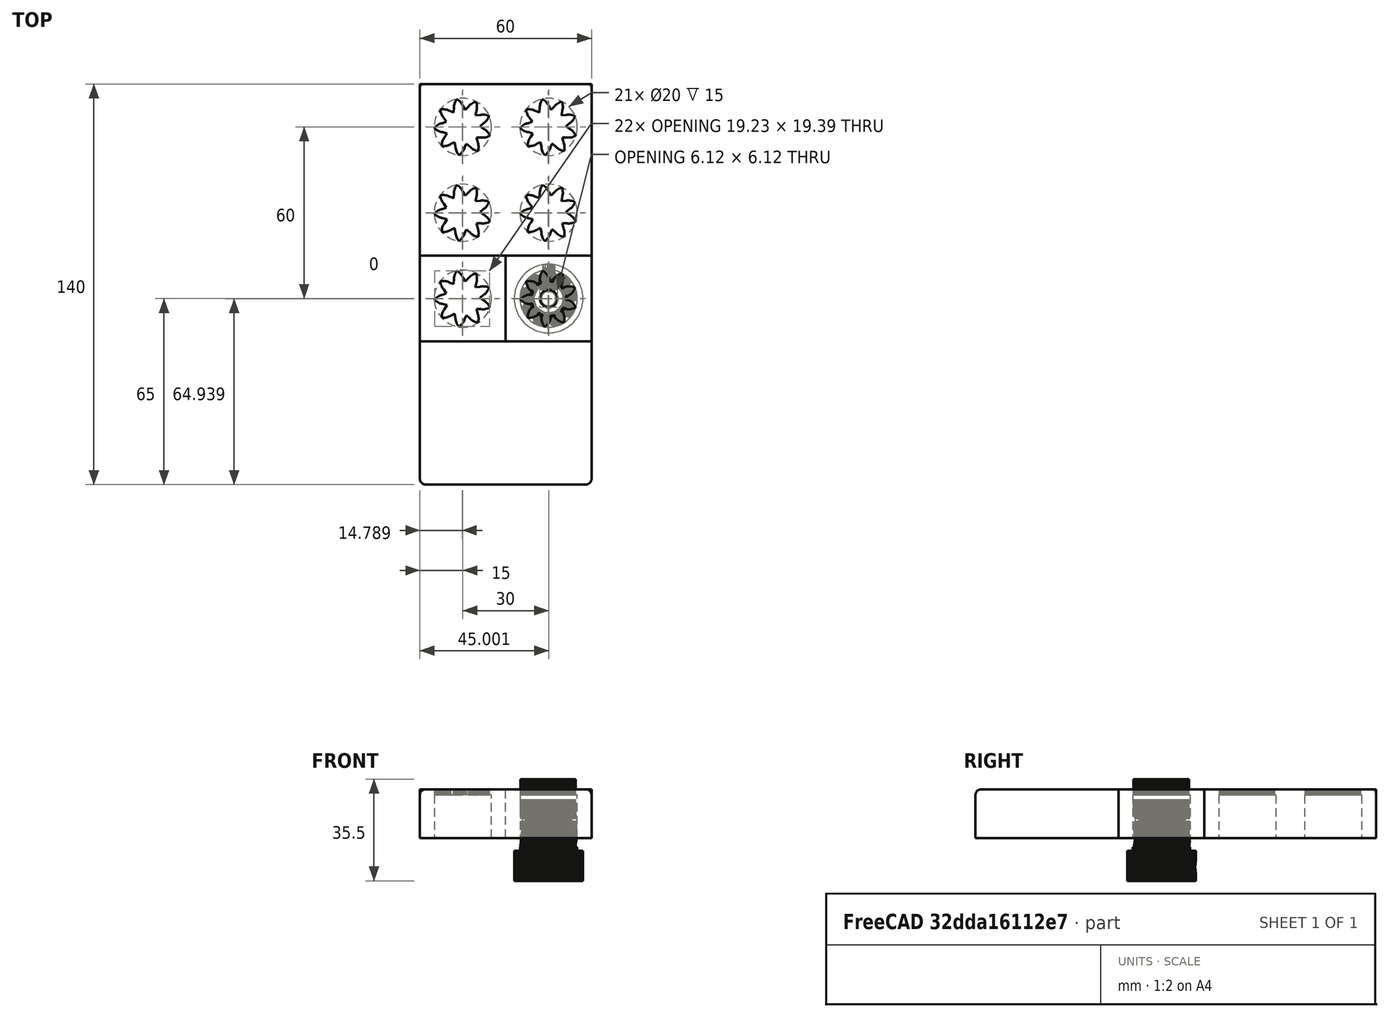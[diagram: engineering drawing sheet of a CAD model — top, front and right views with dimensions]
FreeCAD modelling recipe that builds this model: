
FCSTD DOCUMENT  (FreeCAD 0.17R12018 (Git))
Label: HerringBone6shooter
License: All rights reserved
LicenseURL: http://en.wikipedia.org/wiki/All_rights_reserved
objects: Part::Feature×8, Part::FeaturePython×4, PartDesign::Body×4, Part::MultiFuse×4, PartDesign::Pad×2, Part::Box×2, Sketcher::SketchObject×2, PartDesign::Pocket×2, Mesh::Feature×1, Part::Cylinder×1, Part::Cut×1, PartDesign::ShapeBinder×1, PartDesign::Fillet×1
note: 36 computed .brp shape members not serialized (recipe doc carries the construction recipe); baked Part::Feature solids carry a one-line shape summary decoded from their .brp

FEATURE [Mesh::Feature] herringbone_small_gear_1_1_highres  label="herringbone_small_gear-1.1-highres"
FEATURE [Part::Feature] herringbone_small_gear_1_1_highres001
  shape: bbox 20 x 20 x 21.25 mm, 4060 faces, 0 solids (baked)
FEATURE [Part::Feature] herringbone_small_gear_1_1_highres001_solid  label="herringbone_small_gear_1_1_highres001 (Solid)"
  shape: bbox 20 x 20 x 21.25 mm, 4060 faces (baked)
FEATURE [Part::Feature] herringbone_small_gear_1_1_highres001_solid001  label="herringbone_small_gear_1_1_highres001 (Solid)001"
  shape: bbox 20 x 20 x 21.25 mm, 2720 faces (baked)
FEATURE [Part::FeaturePython] Clone  label="herringbone_small_gear_1_1_highres001 (Solid)002"  # Draft clone (typed FeaturePython)
  AttacherType = Attacher::AttachEngine3D
  Objects = -> [herringbone_small_gear_1_1_highres001_solid001]
  Scale = (1.2,1.2,1.2)
FEATURE [PartDesign::Pad] Pad
  BaseFeature = -> Clone
  Length = 10
  Length2 = 100
  Profile = -> Clone [Face2268]
  Type = 0
FEATURE [PartDesign::Body] Body
  BaseFeature = -> Clone
  Group = -> [Pad]
  Origin = -> Origin
  Tip = -> Pad
FEATURE [Part::Cylinder] Cylinder
  Angle = 360
  AttacherType = Attacher::AttachEngine3D
  Height = 25
  Radius = 3.5
FEATURE [Part::MultiFuse] Fusion
  Shapes = -> [Pad,Cylinder]
FEATURE [Part::Box] Box  label="Cube"
  AttacherType = Attacher::AttachEngine3D
  Height = 2
  Length = 30
  Placement = pos=(-15,-15,12) rot=(0,0,1;0rad)
  Width = 30
FEATURE [Part::Cut] Cut
  Base = -> Box
  Tool = -> Fusion
FEATURE [Part::Box] Box001  label="Cube001"
  AttacherType = Attacher::AttachEngine3D
  Height = 15
  Length = 30
  Placement = pos=(-15,-15,-3) rot=(0,0,1;0rad)
  Width = 30
FEATURE [Part::MultiFuse] Fusion001
  Shapes = -> [Cut,Box001]
FEATURE [Part::Feature] Fusion001001  label="Fusion002"
  shape: bbox 30 x 30 x 17 mm, 277 faces (baked)
FEATURE [PartDesign::ShapeBinder] CopyFusion001001
  Placement = pos=(-15,-15,-3) rot=(0,0,1;0rad)
FEATURE [Sketcher::SketchObject] Sketch
  MapMode = 5
  Placement = pos=(-15,-15,-3) rot=(1,0,0;3.14159rad)
  Support = -> [CopyFusion001001]
  sketch-geometry (1):
    g0: Circle CenterX=15 CenterY=-15 CenterZ=0 NormalX=0 NormalY=0 NormalZ=1 Radius=10
  constraints (3):
    c: DistanceX(g-1,g0) = 15
    c: DistanceY(g0,g-1) = 15
    c: Radius(g0) = 10
FEATURE [PartDesign::Pocket] Pocket
  BaseFeature = -> Fusion001001
  Length = 15
  Profile = -> Sketch
  Type = 0
FEATURE [Sketcher::SketchObject] Sketch001
  MapMode = 5
  Placement = pos=(0,0,14) rot=(0,0,1;0rad)
  Support = -> [Pocket]
  sketch-geometry (29):
    g0: LineSegment StartX=-7.5779 StartY=-1.71709 StartZ=0 EndX=-5.55414 EndY=-2.26969 EndZ=0
    g1: LineSegment StartX=-5.55414 StartY=-2.26969 StartZ=0 EndX=-6.6117 EndY=-4.08146 EndZ=0
    g2: Circle [constr] CenterX=0 CenterY=0 CenterZ=0 NormalX=0 NormalY=0 NormalZ=1 Radius=6
    g3: Circle [constr] CenterX=0 CenterY=0 CenterZ=0 NormalX=0 NormalY=0 NormalZ=1 Radius=7.77
    g4: LineSegment StartX=-6.9128 StartY=3.5477 StartZ=0 EndX=-5.71574 EndY=1.82491 EndZ=0
    g5: LineSegment StartX=-5.71574 StartY=1.82491 StartZ=0 EndX=-7.68965 EndY=1.11453 EndZ=0
    g6: LineSegment StartX=-4.72056 StartY=-6.17165 StartZ=0 EndX=-2.81234 EndY=-5.30007 EndZ=0
    g7: LineSegment StartX=-2.81234 StartY=-5.30007 StartZ=0 EndX=-2.46435 EndY=-7.36885 EndZ=0
    g8: LineSegment StartX=0.369315 StartY=-7.76122 StartZ=0 EndX=1.26636 EndY=-5.86484 EndZ=0
    g9: LineSegment StartX=1.26636 StartY=-5.86484 StartZ=0 EndX=2.86595 EndY=-7.22214 EndZ=0
    g10: LineSegment StartX=5.26463 StartY=-5.71459 StartZ=0 EndX=4.73536 EndY=-3.68462 EndZ=0
    g11: LineSegment StartX=4.73536 StartY=-3.68462 StartZ=0 EndX=6.83315 EndY=-3.69878 EndZ=0
    g12: LineSegment StartX=7.70676 StartY=-0.989318 StartZ=0 EndX=5.9958 EndY=0.224577 EndZ=0
    g13: LineSegment StartX=5.9958 StartY=0.224577 StartZ=0 EndX=7.61116 EndY=1.56306 EndZ=0
    g14: LineSegment StartX=4.82239 StartY=6.09241 StartZ=0 EndX=4.44646 EndY=4.02853 EndZ=0
    g15: LineSegment StartX=4.44646 StartY=4.02853 StartZ=0 EndX=6.53731 EndY=4.19958 EndZ=0
    g16: LineSegment StartX=-0.204433 StartY=7.76731 StartZ=0 EndX=0.830108 EndY=5.9423 EndZ=0
    g17: LineSegment StartX=0.830108 StartY=5.9423 StartZ=0 EndX=2.32517 EndY=7.41394 EndZ=0
    g18: LineSegment StartX=-3.05057 StartY=7.14611 StartZ=0 EndX=-3.2306 EndY=5.05601 EndZ=0
    g19: LineSegment StartX=-3.2306 StartY=5.05601 StartZ=0 EndX=-5.20289 EndY=5.77086 EndZ=0
    g20: ArcOfCircle CenterX=-4.75597 CenterY=3.65797 CenterZ=0 NormalX=0 NormalY=0 NormalZ=1 Radius=2.15964 StartAngle=1.77924 EndAngle=3.19268
    g21: ArcOfCircle CenterX=-1.27944 CenterY=5.862 CenterZ=0 NormalX=0 NormalY=0 NormalZ=1 Radius=2.18766 StartAngle=1.0571 EndAngle=2.51427
    g22: ArcOfCircle CenterX=2.80645 CenterY=5.30319 CenterZ=0 NormalX=0 NormalY=0 NormalZ=1 Radius=2.16492 StartAngle=0.373149 EndAngle=1.79498
    g23: ArcOfCircle CenterX=5.55677 CenterY=2.26326 CenterZ=0 NormalX=0 NormalY=0 NormalZ=1 Radius=2.17044 StartAngle=5.9547 EndAngle=7.38523
    g24: ArcOfCircle CenterX=5.7105 CenterY=-1.84123 CenterZ=0 NormalX=0 NormalY=0 NormalZ=1 Radius=2.17044 StartAngle=5.25602 EndAngle=6.68654
    g25: ArcOfCircle CenterX=3.19272 CenterY=-5.08001 CenterZ=0 NormalX=0 NormalY=0 NormalZ=1 Radius=2.16691 StartAngle=4.56101 EndAngle=5.98598
    g26: ArcOfCircle CenterX=-0.822956 CenterY=-5.94329 CenterZ=0 NormalX=0 NormalY=0 NormalZ=1 Radius=2.17402 StartAngle=3.85673 EndAngle=5.29286
    g27: ArcOfCircle CenterX=-4.44919 CenterY=-4.0255 CenterZ=0 NormalX=0 NormalY=0 NormalZ=1 Radius=2.16323 StartAngle=3.16746 EndAngle=4.58661
    g28: ArcOfCircle CenterX=-5.99533 CenterY=-0.236614 CenterZ=0 NormalX=0 NormalY=0 NormalZ=1 Radius=2.1671 StartAngle=2.4684 EndAngle=3.89367
  constraints (92):
    c: Coincident(g0,g1)
    c: Coincident(g3,g-1)
    c: PointOnObject(g0,g2)
    c: PointOnObject(g0,g3)
    c: PointOnObject(g1,g3)
    c: PointOnObject(g4,g3)
    c: PointOnObject(g4,g2)
    c: Coincident(g4,g5)
    c: PointOnObject(g5,g3)
    c: PointOnObject(g6,g3)
    c: Coincident(g6,g7)
    c: PointOnObject(g7,g3)
    c: PointOnObject(g8,g3)
    c: PointOnObject(g8,g2)
    c: Coincident(g8,g9)
    c: PointOnObject(g9,g3)
    c: PointOnObject(g10,g3)
    c: PointOnObject(g10,g2)
    c: Coincident(g10,g11)
    c: PointOnObject(g11,g3)
    c: PointOnObject(g12,g3)
    c: PointOnObject(g12,g2)
    c: Coincident(g12,g13)
    c: PointOnObject(g13,g3)
    c: PointOnObject(g14,g3)
    c: PointOnObject(g14,g2)
    c: Coincident(g14,g15)
    c: PointOnObject(g15,g3)
    c: PointOnObject(g16,g3)
    c: PointOnObject(g16,g2)
    c: Coincident(g16,g17)
    c: PointOnObject(g17,g3)
    c: PointOnObject(g18,g3)
    c: PointOnObject(g18,g2)
    c: Coincident(g18,g19)
    c: PointOnObject(g19,g3)
    c: Angle(g0,g1) = 1.309
    c: Angle(g4,g5) = 1.309
    c: Angle(g18,g19) = 1.309
    c: Angle(g17,g16) = 1.309
    c: Angle(g15,g14) = 1.309
    c: Angle(g12,g13) = 1.309
    c: Angle(g10,g11) = 1.309
    c: Angle(g8,g9) = 1.309
    c: Angle(g6,g7) = 1.309
    c: Radius(g2) = 6
    c: Coincident(g2,g-1)
    c: Radius(g3) = 7.77
    c: PointOnObject(g20,g2)
    c: Coincident(g20,g4)
    c: Coincident(g20,g19)
    c: PointOnObject(g21,g2)
    c: Coincident(g21,g16)
    c: Coincident(g18,g21)
    c: PointOnObject(g22,g2)
    c: Coincident(g22,g17)
    c: Coincident(g22,g14)
    c: PointOnObject(g23,g2)
    c: Coincident(g23,g15)
    c: Coincident(g23,g13)
    c: PointOnObject(g24,g2)
    c: Coincident(g24,g12)
    c: Coincident(g24,g11)
    c: PointOnObject(g25,g2)
    c: Coincident(g25,g10)
    c: Coincident(g25,g9)
    c: PointOnObject(g26,g2)
    c: Coincident(g26,g7)
    c: Coincident(g26,g8)
    c: PointOnObject(g27,g2)
    c: Coincident(g27,g1)
    c: Coincident(g27,g6)
    c: PointOnObject(g28,g2)
    c: Coincident(g28,g5)
    c: Coincident(g28,g0)
    c: Equal(g5,g4)
    c: Equal(g4,g19)
    c: Equal(g19,g18)
    c: Equal(g18,g16)
    c: Equal(g16,g17)
    c: Equal(g17,g14)
    c: Equal(g14,g15)
    c: Equal(g15,g13)
    c: Equal(g13,g12)
    c: Equal(g12,g11)
    c: Equal(g11,g10)
    c: Equal(g10,g9)
    c: Equal(g9,g8)
    c: Equal(g8,g7)
    c: Equal(g7,g6)
    c: Equal(g6,g1)
    c: Equal(g1,g0)
FEATURE [PartDesign::Pocket] Pocket001
  BaseFeature = -> Pocket
  Length = 5
  Profile = -> Sketch001
  Type = 0
FEATURE [PartDesign::Body] Body001
  BaseFeature = -> Fusion001001
  Group = -> [CopyFusion001001,Sketch,Pocket,Sketch001,Pocket001]
  Origin = -> Origin001
  Tip = -> Pocket001
FEATURE [Part::Feature] Pocket001001  label="Pocket002"
  shape: bbox 30 x 30 x 17 mm, 201 faces (baked)
FEATURE [PartDesign::Body] Body002
  BaseFeature = -> Pocket001001
  Origin = -> Origin002
  Tip = -> Pocket001001
FEATURE [Part::FeaturePython] Clone001  label="Pocket003"  # Draft clone (typed FeaturePython)
  AttacherType = Attacher::AttachEngine3D
  Objects = -> [Pocket001001]
  Placement = pos=(-30,0,0) rot=(0,0,1;0rad)
  Scale = (1,1,1)
FEATURE [Part::MultiFuse] Fusion001002
  Shapes = -> [Pocket001001,Clone001]
FEATURE [Part::Feature] Fusion001002001  label="Fusion001003"
  shape: bbox 60 x 30 x 17 mm, 396 faces (baked)
FEATURE [Part::FeaturePython] Clone002  label="Fusion001004"  # Draft clone (typed FeaturePython)
  AttacherType = Attacher::AttachEngine3D
  Objects = -> [Fusion001002001]
  Placement = pos=(0,30,0) rot=(0,0,1;0rad)
  Scale = (1,1,1)
FEATURE [Part::FeaturePython] Clone003  label="Fusion001005"  # Draft clone (typed FeaturePython)
  AttacherType = Attacher::AttachEngine3D
  Objects = -> [Clone002]
  Placement = pos=(0,60,0) rot=(0,0,1;0rad)
  Scale = (1,1,1)
FEATURE [Part::MultiFuse] Fusion001002002
  Shapes = -> [Fusion001002001,Clone002,Clone003]
FEATURE [Part::Feature] Fusion001002002001  label="Fusion001002003"
  shape: bbox 60 x 90 x 17 mm, 1176 faces (baked)
FEATURE [PartDesign::Pad] Pad001
  BaseFeature = -> Fusion001002002001
  Length = 50
  Length2 = 100
  Profile = -> Fusion001002002001 [Face1]
  Type = 0
FEATURE [PartDesign::Fillet] Fillet
  Base = -> Pad001 [Face6,Edge26,Edge10,Edge7,Edge24,Edge23]
  BaseFeature = -> Pad001
  Radius = 2
FEATURE [PartDesign::Body] Body003
  BaseFeature = -> Fusion001002002001
  Group = -> [Pad001,Fillet]
  Origin = -> Origin003
  Tip = -> Fillet
FEATURE [Part::Feature] Fillet001
  shape: bbox 60 x 140 x 17 mm, 1188 faces (baked)
